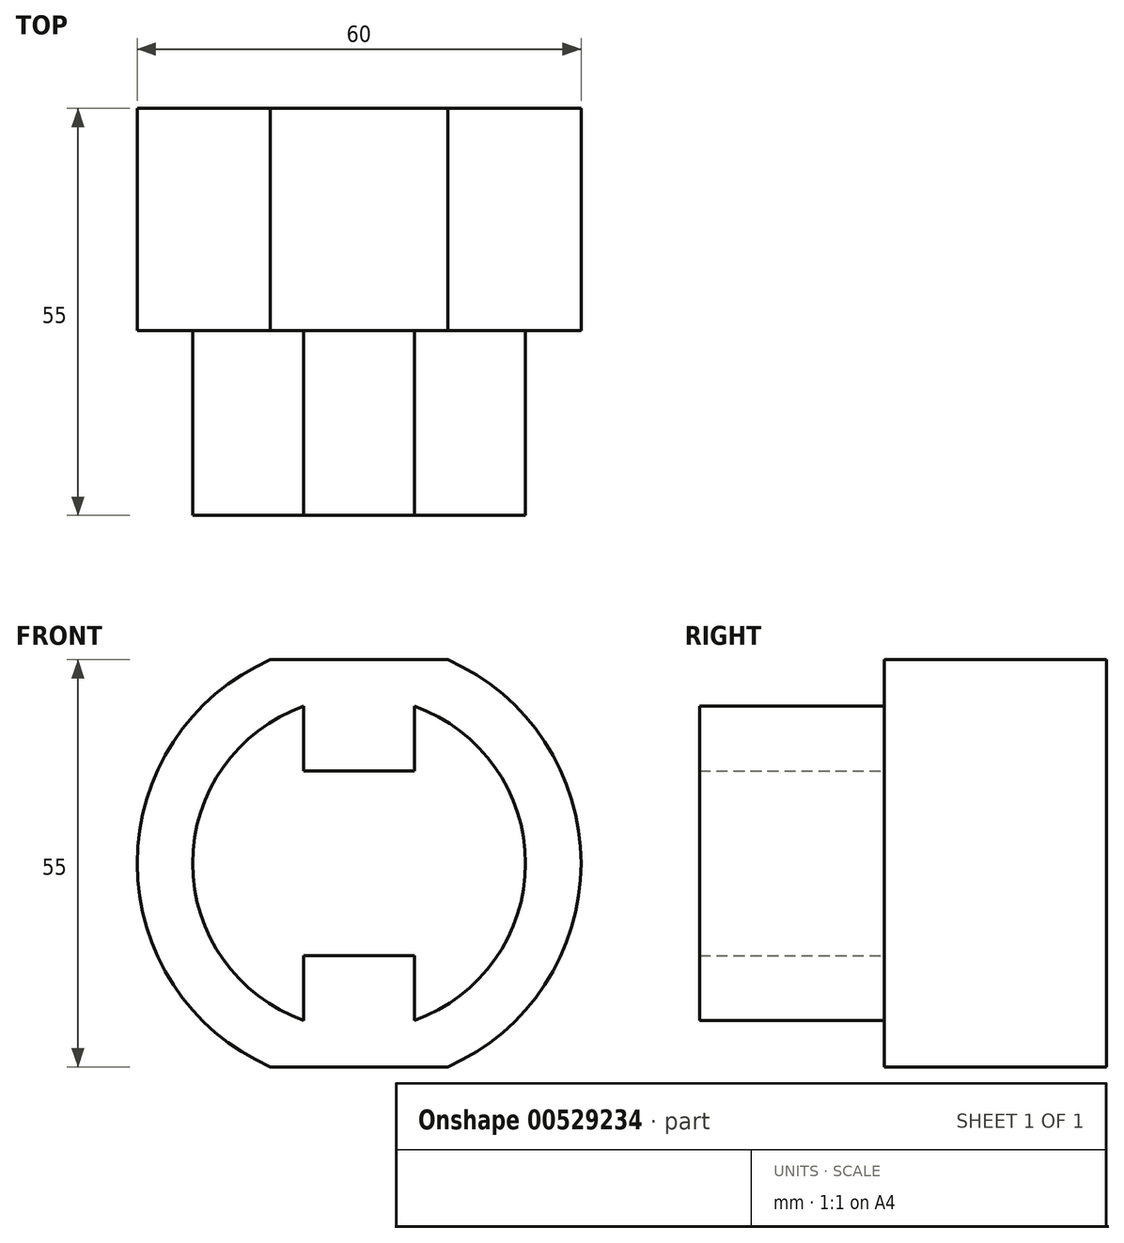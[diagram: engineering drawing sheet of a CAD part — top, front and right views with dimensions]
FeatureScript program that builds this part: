
annotation { "Feature Type Name" : "Feature", "Feature Type Description" : "" }
export const myFeature = defineFeature(function(context is Context, id is Id, definition is map)
    precondition{}
    {
        {
            var Q0;
            Q0=qCreatedBy(makeId("Front.planeOp"),FACE);
            var sketch = newSketch(context, id + "F0", { "sketchPlane" : qUnion([Q0])});
            skCircle(sketch, "E0", {"center": v(0, 0) * mm, "radius": 30 * mm});
            skLineSegment(sketch, "E1", {"start": v(-11.99, 27.5) * mm, "end": v(11.99, 27.5) * mm});
            skLineSegment(sketch, "E2", {"start": v(-11.99, -27.5) * mm, "end": v(11.99, -27.5) * mm});
            skLineSegment(sketch, "E3", {"start": v(-30, 0) * mm, "end": v(30, 0) * mm, "construction": true});
            skSolve(sketch);
        }
        {
            var Q0;
            {var subQ0=sQuery(id+"F0.wireOp",EDGE,"E1");Q0=makeQuery(id+"F0.imprint","IMPRINT",FACE,{"disambiguationData":[TD([[makeQuery(id+"F0.imprint","IMPRINT",EDGE,{"derivedFrom":subQ0}),-1.0]])]});}
            extrude(context, id + "F1", {"entities" : qUnion([Q0]), "endBound" : BoundingType.SYMMETRIC, "depth" : 30 * mm, "offsetDistance" : 25 * mm});
        }
        {
            var Q0;
            Q0=makeQuery(id+"F1.opExtrude","CAP_FACE",FACE,{"disambiguationData":[OSD([sQuery(id+"F0.wireOp",EDGE,"E0"),sQuery(id+"F0.wireOp",EDGE,"E1"),sQuery(id+"F0.wireOp",EDGE,"E2")])],"isStart":false});
            var sketch = newSketch(context, id + "F2", { "sketchPlane" : qUnion([Q0])});
            skCircle(sketch, "E4", {"center": v(0, 0) * mm, "radius": 22.5 * mm});
            skLineSegment(sketch, "E5", {"start": v(0, 22.5) * mm, "end": v(0, -22.5) * mm, "construction": true});
            skLineSegment(sketch, "E6", {"start": v(-7.5, 21.21) * mm, "end": v(-7.5, 12.5) * mm});
            skLineSegment(sketch, "E7", {"start": v(-7.5, 12.5) * mm, "end": v(7.5, 12.5) * mm});
            skLineSegment(sketch, "E8", {"start": v(7.5, 12.5) * mm, "end": v(7.5, 21.21) * mm});
            skLineSegment(sketch, "E9", {"start": v(-7.5, -21.21) * mm, "end": v(-7.5, -12.5) * mm});
            skLineSegment(sketch, "E10", {"start": v(-7.5, -12.5) * mm, "end": v(7.5, -12.5) * mm});
            skLineSegment(sketch, "E11", {"start": v(7.5, -12.5) * mm, "end": v(7.5, -21.21) * mm});
            skLineSegment(sketch, "E12", {"start": v(-22.5, 0) * mm, "end": v(22.5, 0) * mm, "construction": true});
            skSolve(sketch);
        }
        {
            var Q0;
            {var subQ0=sQuery(id+"F2.wireOp",EDGE,"E6");Q0=makeQuery(id+"F2.imprint","IMPRINT",FACE,{"disambiguationData":[TD([[makeQuery(id+"F2.imprint","IMPRINT",EDGE,{"derivedFrom":subQ0}),-1.0]])]});}
            extrude(context, id + "F3", {"entities" : qUnion([Q0]), "operationType" : NewBodyOperationType.ADD, "depth" : 25 * mm, "offsetDistance" : 25 * mm});
        }
    });
